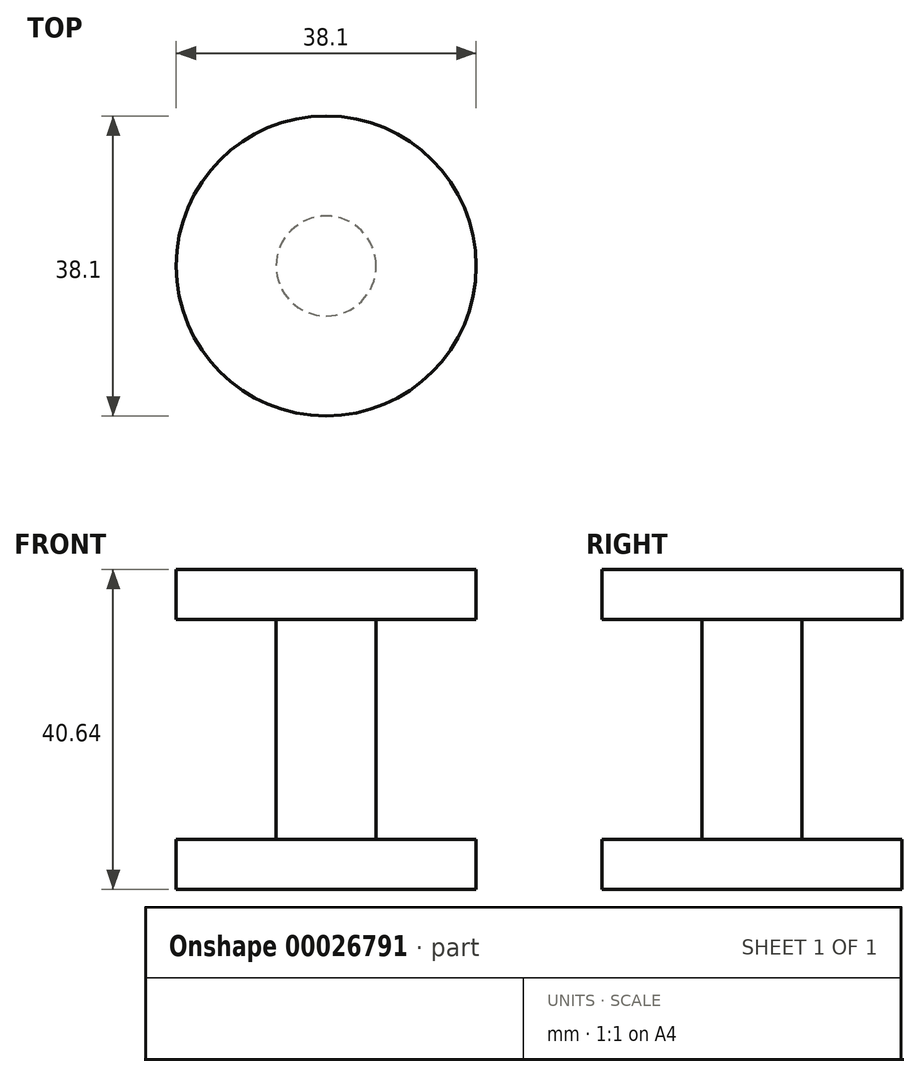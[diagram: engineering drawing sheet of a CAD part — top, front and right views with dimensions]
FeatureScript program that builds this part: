
annotation { "Feature Type Name" : "Feature", "Feature Type Description" : "" }
export const myFeature = defineFeature(function(context is Context, id is Id, definition is map)
    precondition{}
    {
        {
            var Q0;
            Q0=qCreatedBy(makeId("Top.planeOp"),FACE);
            var sketch = newSketch(context, id + "F0", { "sketchPlane" : qUnion([Q0])});
            skCircle(sketch, "E0", {"center": v(-5.09, 11.7) * mm, "radius": 19.05 * mm});
            skCircle(sketch, "E1", {"center": v(-5.09, 11.7) * mm, "radius": 6.35 * mm});
            skSolve(sketch);
        }
        {
            var Q0;
            Q0=makeQuery(id+"F0.imprint","IMPRINT",FACE,{"disambiguationData":[TD([[makeQuery(id+"F0.imprint","IMPRINT",EDGE,{"derivedFrom":sQuery(id+"F0.wireOp",EDGE,"E1")}),1.0]])]});
            var Q1;
            Q1=makeQuery(id+"F0.imprint","IMPRINT",FACE,{"disambiguationData":[TD([[makeQuery(id+"F0.imprint","IMPRINT",EDGE,{"derivedFrom":sQuery(id+"F0.wireOp",EDGE,"E0")}),1.0]])]});
            extrude(context, id + "F1", {"entities" : qUnion([Q0, Q1]), "endBound" : BoundingType.SYMMETRIC, "depth" : 40.64 * mm});
        }
        {
            var Q0;
            Q0=makeQuery(id+"F0.imprint","IMPRINT",FACE,{"disambiguationData":[TD([[makeQuery(id+"F0.imprint","IMPRINT",EDGE,{"derivedFrom":sQuery(id+"F0.wireOp",EDGE,"E0")}),1.0]])]});
            extrude(context, id + "F2", {"entities" : qUnion([Q0]), "operationType" : NewBodyOperationType.REMOVE, "endBound" : BoundingType.SYMMETRIC, "oppositeDirection" : true, "depth" : 27.94 * mm});
        }
    });
